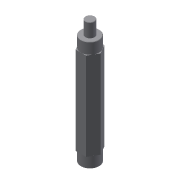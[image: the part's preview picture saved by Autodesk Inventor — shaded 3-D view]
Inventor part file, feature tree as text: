
AUTODESK INVENTOR PART (.ipt)
format: ipt  version: 2013 (Build 170138000, 138)  size: 101,376 bytes
history: native  units: in
note: dims shown in document units (in); Inventor stores cm internally (conversion verified against a paired STEP export)
features: chamfer x1, other x1, imported_body x1
ambient origin geometry x8: Origin, YZ Plane, XZ Plane, XY Plane, X Axis, Y Axis, Z Axis, Center Point
feature tree (3):
  chamfer  "Chamfer4"  [1 undecoded]
  other  "446 Cluster Hex Shaft 5001"
  imported_body  "Base1"
note: 1 required parameter value undecoded (feature->parameter linkage not recoverable at this tier; creation-order binding heuristic only, values carry confidence <= 0.55)
